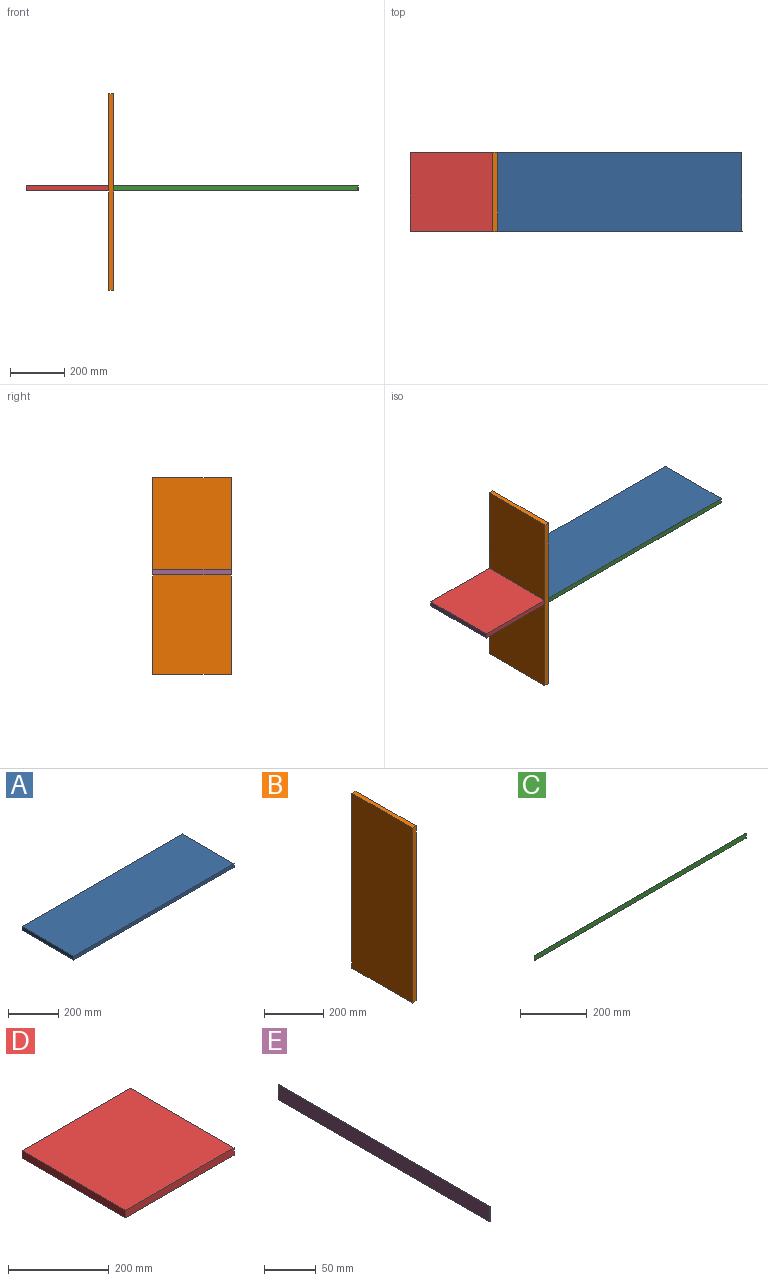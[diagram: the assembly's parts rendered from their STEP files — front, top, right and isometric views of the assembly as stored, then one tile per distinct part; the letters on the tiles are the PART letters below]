
ASSEMBLY  parts=5 mates=4
PART A: 6 faces, bbox 900x290x18 mm
  f0: plane 900x18mm, normal (0,1,0), area 16200mm2, adj f1,f3,f4,f5
  f1: plane 290x18mm, normal (-1,0,0), area 5220mm2, adj f0,f2,f4,f5
  f2: plane 900x18mm, normal (0,-1,0), area 16200mm2, adj f1,f3,f4,f5
  f3: plane 290x18mm, normal (1,0,0), area 5220mm2, adj f0,f2,f4,f5
  f4: plane 900x290mm, normal (0,0,1), area 261000mm2, adj f0,f1,f2,f3
  f5: plane 900x290mm, normal (0,0,-1), area 261000mm2, adj f0,f1,f2,f3
PART B: 6 faces, bbox 18x290x725 mm
  f0: plane 725x18mm, normal (0,1,0), area 13050mm2, adj f1,f3,f4,f5
  f1: plane 725x290mm, normal (-1,0,0), area 210250mm2, adj f0,f2,f4,f5
  f2: plane 725x18mm, normal (0,-1,0), area 13050mm2, adj f1,f3,f4,f5
  f3: plane 725x290mm, normal (1,0,0), area 210250mm2, adj f0,f2,f4,f5
  f4: plane 290x18mm, normal (0,0,1), area 5220mm2, adj f0,f1,f2,f3
  f5: plane 290x18mm, normal (0,0,-1), area 5220mm2, adj f0,f1,f2,f3
PART C: 6 faces, bbox 900x0.8x18 mm
  f0: plane 900x18mm, normal (0,1,0), area 16200mm2, adj f1,f3,f4,f5
  f1: plane 18x0.8mm, normal (-1,0,0), area 14.4mm2, adj f0,f2,f4,f5
  f2: plane 900x18mm, normal (0,-1,0), area 16200mm2, adj f1,f3,f4,f5
  f3: plane 18x0.8mm, normal (1,0,0), area 14.4mm2, adj f0,f2,f4,f5
  f4: plane 900x0.8mm, normal (0,0,1), area 720mm2, adj f0,f1,f2,f3
  f5: plane 900x0.8mm, normal (0,0,-1), area 720mm2, adj f0,f1,f2,f3
PART D: 6 faces, bbox 304x290x18 mm
  f0: plane 304x18mm, normal (0,1,0), area 5472mm2, adj f1,f3,f4,f5
  f1: plane 290x18mm, normal (-1,0,0), area 5220mm2, adj f0,f2,f4,f5
  f2: plane 304x18mm, normal (0,-1,0), area 5472mm2, adj f1,f3,f4,f5
  f3: plane 290x18mm, normal (1,0,0), area 5220mm2, adj f0,f2,f4,f5
  f4: plane 304x290mm, normal (0,0,1), area 88160mm2, adj f0,f1,f2,f3
  f5: plane 304x290mm, normal (0,0,-1), area 88160mm2, adj f0,f1,f2,f3
PART E: 6 faces, bbox 0.8x290x18 mm
  f0: plane 18x0.8mm, normal (0,1,0), area 14.4mm2, adj f1,f3,f4,f5
  f1: plane 290x18mm, normal (-1,0,0), area 5220mm2, adj f0,f2,f4,f5
  f2: plane 18x0.8mm, normal (0,-1,0), area 14.4mm2, adj f1,f3,f4,f5
  f3: plane 290x18mm, normal (1,0,0), area 5220mm2, adj f0,f2,f4,f5
  f4: plane 290x0.8mm, normal (0,0,1), area 232mm2, adj f0,f1,f2,f3
  f5: plane 290x0.8mm, normal (0,0,-1), area 232mm2, adj f0,f1,f2,f3
PLACE A t=(1000.24,515.22,-295.52)mm
PLACE B t=(571.75,579.11,-662.52)mm
PLACE C t=(1002.54,433.19,-295.52)mm
PLACE D t=(333.49,529.03,-295.52)mm
PLACE E t=(281.68,554.79,-295.52)mm
MATE fastened B.f3 <-> A.f1  axis (1,0,0) through (550.32,676.92,62.48)mm
MATE fastened A.f2 <-> C.f0  axis (0,-1,0) through (1000.32,386.92,-286.52)mm
MATE fastened D.f1 <-> E.f3  axis (-1,0,0) through (228.32,531.92,-286.52)mm
MATE fastened B.f1 <-> D.f3  axis (-1,0,0) through (532.32,676.92,62.48)mm
